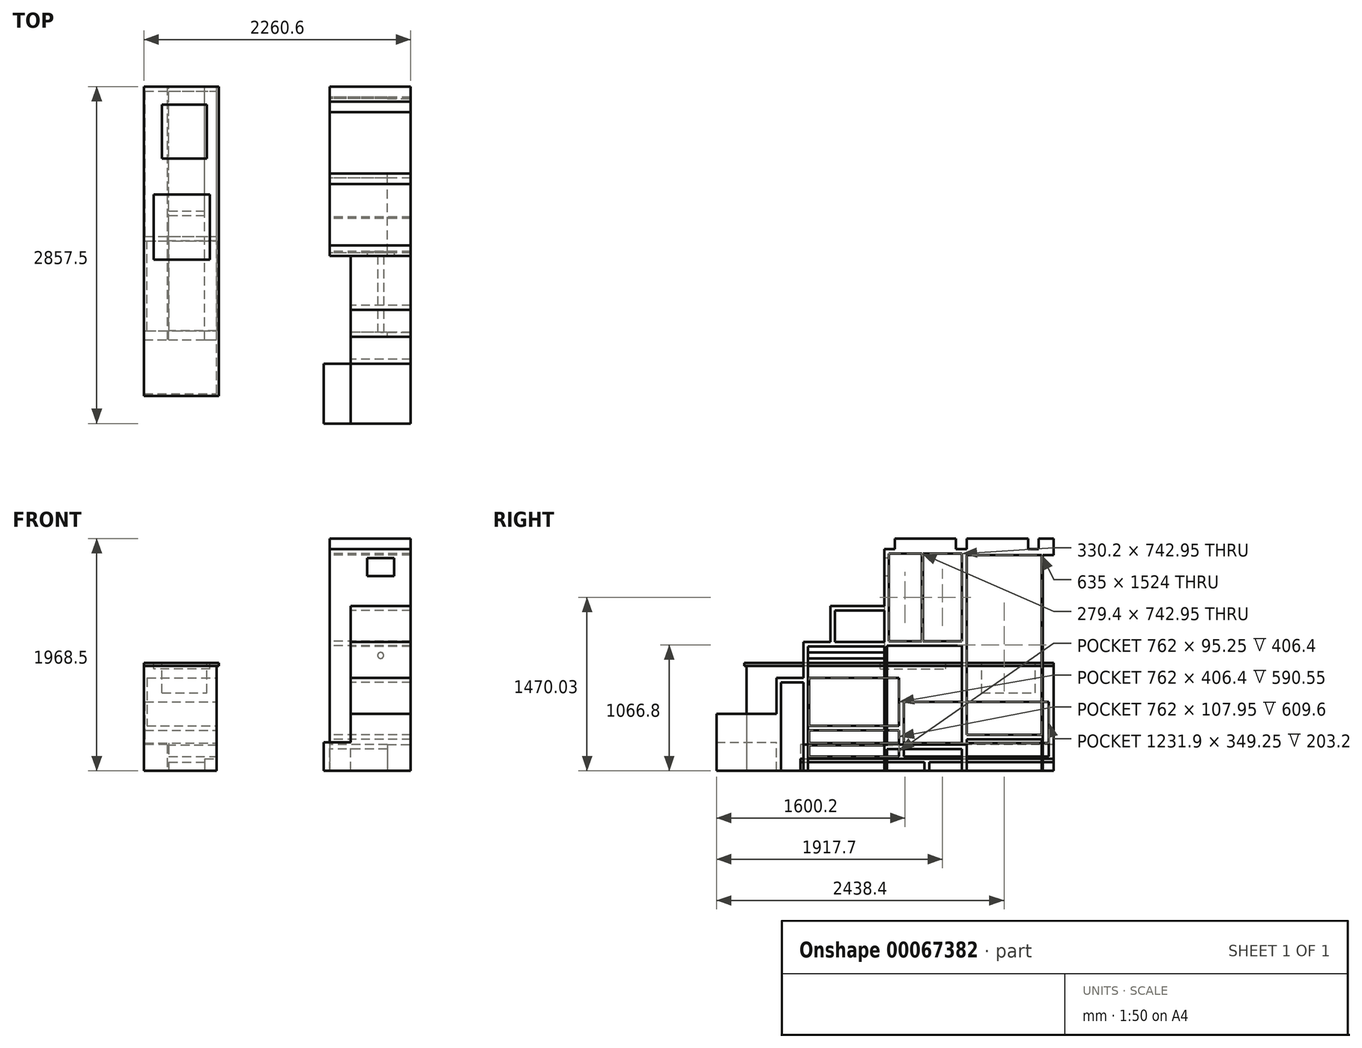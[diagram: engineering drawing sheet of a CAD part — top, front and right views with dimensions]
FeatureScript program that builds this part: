
annotation { "Feature Type Name" : "Feature", "Feature Type Description" : "" }
export const myFeature = defineFeature(function(context is Context, id is Id, definition is map)
    precondition{}
    {
        {
            var Q0;
            Q0=qCreatedBy(makeId("Top.planeOp"),FACE);
            var sketch = newSketch(context, id + "F0", { "sketchPlane" : qUnion([Q0])});
            skLineSegment(sketch, "E0", {"start": v(0, 0) * mm, "end": v(635, 0) * mm});
            skLineSegment(sketch, "E1", {"start": v(635, 0) * mm, "end": v(635, -2146.3) * mm});
            skLineSegment(sketch, "E2", {"start": v(635, -2146.3) * mm, "end": v(0, -2146.3) * mm});
            skLineSegment(sketch, "E3", {"start": v(0, -2146.3) * mm, "end": v(0, 0) * mm});
            skLineSegment(sketch, "E4", {"start": v(0, -2146.3) * mm, "end": v(0, -3213.1) * mm, "construction": true});
            skLineSegment(sketch, "E5", {"start": v(0, -3213.1) * mm, "end": v(635, -3213.1) * mm, "construction": true});
            skLineSegment(sketch, "E6", {"start": v(635, -3213.1) * mm, "end": v(635, -2146.3) * mm, "construction": true});
            skSolve(sketch);
        }
        {
            var Q0;
            Q0 = qSketchRegion(id + "F0", true);
            extrude(context, id + "F1", {"entities" : qUnion([Q0]), "depth" : 914.4 * mm});
        }
        {
            var Q0;
            Q0=makeQuery(id+"F1.opExtrude","SWEPT_FACE",FACE,{"disambiguationData":[OSD([sQuery(id+"F0.wireOp",EDGE,"E2")])]});
            var sketch = newSketch(context, id + "F2", { "sketchPlane" : qUnion([Q0])});
            skLineSegment(sketch, "E7.bottom", {"start": v(0, 0) * mm, "end": v(196.85, 0) * mm});
            skLineSegment(sketch, "E7.top", {"start": v(0, 222.25) * mm, "end": v(196.85, 222.25) * mm});
            skLineSegment(sketch, "E7.left", {"start": v(0, 0) * mm, "end": v(0, 222.25) * mm});
            skLineSegment(sketch, "E7.right", {"start": v(196.85, 0) * mm, "end": v(196.85, 222.25) * mm});
            skSolve(sketch);
        }
        {
            var Q0;
            Q0 = qSketchRegion(id + "F2", true);
            extrude(context, id + "F3", {"entities" : qUnion([Q0]), "operationType" : NewBodyOperationType.REMOVE, "oppositeDirection" : true, "depth" : 2260.6 * mm});
        }
        {
            var Q0;
            Q0=makeQuery(id+"F1.opExtrude","CAP_FACE",FACE,{"disambiguationData":[OSD([sQuery(id+"F0.wireOp",EDGE,"E0"),sQuery(id+"F0.wireOp",EDGE,"L1nPwehb-1XyT-S8cI-bZGU-SJZBOORDtoRi"),sQuery(id+"F0.wireOp",EDGE,"4dkKAuYr-NdsE-A3nL-FX6l-y6qERZtvD3tl"),sQuery(id+"F0.wireOp",EDGE,"E1"),sQuery(id+"F0.wireOp",EDGE,"E2"),sQuery(id+"F0.wireOp",EDGE,"E3")])],"isStart":true});
            var sketch = newSketch(context, id + "F4", { "sketchPlane" : qUnion([Q0])});
            skLineSegment(sketch, "E8", {"start": v(615.95, 2146.3) * mm, "end": v(615.95, 0) * mm});
            skLineSegment(sketch, "E9", {"start": v(615.95, 0) * mm, "end": v(635, 0) * mm});
            skLineSegment(sketch, "E10", {"start": v(635, 0) * mm, "end": v(635, 2146.3) * mm});
            skLineSegment(sketch, "E11", {"start": v(635, 2146.3) * mm, "end": v(615.95, 2146.3) * mm});
            skSolve(sketch);
        }
        {
            var Q0;
            Q0 = qSketchRegion(id + "F4", true);
            extrude(context, id + "F5", {"entities" : qUnion([Q0]), "operationType" : NewBodyOperationType.REMOVE, "oppositeDirection" : true, "depth" : 889 * mm});
        }
        {
            var Q0;
            Q0=makeQuery(id+"F1.opExtrude","SWEPT_FACE",FACE,{"disambiguationData":[OSD([sQuery(id+"F0.wireOp",EDGE,"E2")])]});
            var sketch = newSketch(context, id + "F6", { "sketchPlane" : qUnion([Q0])});
            skLineSegment(sketch, "E12.bottom", {"start": v(635, 889) * mm, "end": v(0, 889) * mm});
            skLineSegment(sketch, "E12.top", {"start": v(635, 914.4) * mm, "end": v(0, 914.4) * mm});
            skLineSegment(sketch, "E12.left", {"start": v(635, 889) * mm, "end": v(635, 914.4) * mm});
            skLineSegment(sketch, "E12.right", {"start": v(0, 889) * mm, "end": v(0, 914.4) * mm});
            skSolve(sketch);
        }
        {
            var Q0;
            Q0=makeQuery(id+"F1.opExtrude","CAP_FACE",FACE,{"disambiguationData":[OSD([sQuery(id+"F0.wireOp",EDGE,"E0"),sQuery(id+"F0.wireOp",EDGE,"L1nPwehb-1XyT-S8cI-bZGU-SJZBOORDtoRi"),sQuery(id+"F0.wireOp",EDGE,"4dkKAuYr-NdsE-A3nL-FX6l-y6qERZtvD3tl"),sQuery(id+"F0.wireOp",EDGE,"E1"),sQuery(id+"F0.wireOp",EDGE,"E2"),sQuery(id+"F0.wireOp",EDGE,"E3")])],"isStart":false});
            var sketch = newSketch(context, id + "F7", { "sketchPlane" : qUnion([Q0])});
            skLineSegment(sketch, "E13.bottom", {"start": v(558.8, -1466.85) * mm, "end": v(82.55, -1466.85) * mm});
            skLineSegment(sketch, "E13.top", {"start": v(558.8, -914.4) * mm, "end": v(82.55, -914.4) * mm});
            skLineSegment(sketch, "E13.left", {"start": v(558.8, -1466.85) * mm, "end": v(558.8, -914.4) * mm});
            skLineSegment(sketch, "E13.right", {"start": v(82.55, -1466.85) * mm, "end": v(82.55, -914.4) * mm});
            skSolve(sketch);
        }
        {
            var Q0;
            Q0 = qSketchRegion(id + "F7", true);
            extrude(context, id + "F8", {"entities" : qUnion([Q0]), "operationType" : NewBodyOperationType.REMOVE, "oppositeDirection" : true, "depth" : 50.8 * mm});
        }
        {
            var Q0;
            Q0=makeQuery(id+"F1.opExtrude","SWEPT_FACE",FACE,{"disambiguationData":[OSD([sQuery(id+"F0.wireOp",EDGE,"E1")])]});
            var sketch = newSketch(context, id + "F9", { "sketchPlane" : qUnion([Q0])});
            skLineSegment(sketch, "E14.bottom", {"start": v(-2070.1, 787.4) * mm, "end": v(-1308.1, 787.4) * mm});
            skLineSegment(sketch, "E14.top", {"start": v(-2070.1, 381) * mm, "end": v(-1308.1, 381) * mm});
            skLineSegment(sketch, "E14.left", {"start": v(-2070.1, 787.4) * mm, "end": v(-2070.1, 381) * mm});
            skLineSegment(sketch, "E14.right", {"start": v(-1308.1, 787.4) * mm, "end": v(-1308.1, 381) * mm});
            skLineSegment(sketch, "E15", {"start": v(-1689.1, 787.4) * mm, "end": v(-1190.62, 914.4) * mm, "construction": true});
            skSolve(sketch);
        }
        {
            var Q0;
            Q0 = qSketchRegion(id + "F9", true);
            extrude(context, id + "F10", {"entities" : qUnion([Q0]), "operationType" : NewBodyOperationType.REMOVE, "oppositeDirection" : true, "depth" : 609.6 * mm});
        }
        {
            var Q0;
            Q0=makeQuery(id+"F6nNggxzTz6gh16_2.boolean.opBoolean","MERGE",FACE,{"derivedFrom":[makeQuery(id+"F1.opExtrude","CAP_FACE",FACE,{"disambiguationData":[OSD([sQuery(id+"F0.wireOp",EDGE,"E0"),sQuery(id+"F0.wireOp",EDGE,"L1nPwehb-1XyT-S8cI-bZGU-SJZBOORDtoRi"),sQuery(id+"F0.wireOp",EDGE,"4dkKAuYr-NdsE-A3nL-FX6l-y6qERZtvD3tl"),sQuery(id+"F0.wireOp",EDGE,"E1"),sQuery(id+"F0.wireOp",EDGE,"E2"),sQuery(id+"F0.wireOp",EDGE,"E3")])],"isStart":false}),makeQuery(id+"F6nNggxzTz6gh16_2.opExtrude","SWEPT_FACE",FACE,{"disambiguationData":[OSD([sQuery(id+"F6.wireOp",EDGE,"E12.top")])]})]});
            var sketch = newSketch(context, id + "F11", { "sketchPlane" : qUnion([Q0])});
            skLineSegment(sketch, "E16.bottom", {"start": v(152.4, -609.6) * mm, "end": v(533.4, -609.6) * mm});
            skLineSegment(sketch, "E16.top", {"start": v(152.4, -152.4) * mm, "end": v(533.4, -152.4) * mm});
            skLineSegment(sketch, "E16.left", {"start": v(152.4, -609.6) * mm, "end": v(152.4, -152.4) * mm});
            skLineSegment(sketch, "E16.right", {"start": v(533.4, -609.6) * mm, "end": v(533.4, -152.4) * mm});
            skSolve(sketch);
        }
        {
            var Q0;
            Q0 = qSketchRegion(id + "F11", true);
            extrude(context, id + "F12", {"entities" : qUnion([Q0]), "operationType" : NewBodyOperationType.REMOVE, "oppositeDirection" : true, "depth" : 254 * mm});
        }
        {
            var Q0;
            Q0=makeQuery(id+"F5.boolean.opBoolean","COPY",FACE,{"derivedFrom":makeQuery(id+"F5.opExtrude","SWEPT_FACE",FACE,{"disambiguationData":[OSD([sQuery(id+"F4.wireOp",EDGE,"E8")])]})});
            var sketch = newSketch(context, id + "F13", { "sketchPlane" : qUnion([Q0])});
            skLineSegment(sketch, "E17.bottom", {"start": v(-2146.3, 0) * mm, "end": v(0, 0) * mm});
            skLineSegment(sketch, "E17.top", {"start": v(-2146.3, 101.6) * mm, "end": v(0, 101.6) * mm});
            skLineSegment(sketch, "E17.left", {"start": v(-2146.3, 0) * mm, "end": v(-2146.3, 101.6) * mm});
            skLineSegment(sketch, "E17.right", {"start": v(0, 0) * mm, "end": v(0, 101.6) * mm});
            skSolve(sketch);
        }
        {
            var Q0;
            Q0 = qSketchRegion(id + "F13", true);
            extrude(context, id + "F14", {"entities" : qUnion([Q0]), "operationType" : NewBodyOperationType.REMOVE, "oppositeDirection" : true, "depth" : 101.6 * mm});
        }
        {
            var Q0;
            Q0=makeQuery(id+"F5.boolean.opBoolean","COPY",FACE,{"derivedFrom":makeQuery(id+"F5.opExtrude","SWEPT_FACE",FACE,{"disambiguationData":[OSD([sQuery(id+"F4.wireOp",EDGE,"E8")])]})});
            var sketch = newSketch(context, id + "F15", { "sketchPlane" : qUnion([Q0])});
            skLineSegment(sketch, "E18.bottom", {"start": v(-2070.1, 342.9) * mm, "end": v(-1308.1, 342.9) * mm});
            skLineSegment(sketch, "E18.top", {"start": v(-2070.1, 120.65) * mm, "end": v(-1308.1, 120.65) * mm});
            skLineSegment(sketch, "E18.left", {"start": v(-2070.1, 342.9) * mm, "end": v(-2070.1, 120.65) * mm});
            skLineSegment(sketch, "E18.right", {"start": v(-1308.1, 342.9) * mm, "end": v(-1308.1, 120.65) * mm});
            skLineSegment(sketch, "E19.bottom", {"start": v(-1270, 584.2) * mm, "end": v(-38.1, 584.2) * mm});
            skLineSegment(sketch, "E19.top", {"start": v(-1270, 120.65) * mm, "end": v(-38.1, 120.65) * mm});
            skLineSegment(sketch, "E19.left", {"start": v(-1270, 584.2) * mm, "end": v(-1270, 120.65) * mm});
            skLineSegment(sketch, "E19.right", {"start": v(-38.1, 584.2) * mm, "end": v(-38.1, 120.65) * mm});
            skSolve(sketch);
        }
        {
            var Q0;
            Q0 = qSketchRegion(id + "F15", true);
            extrude(context, id + "F16", {"entities" : qUnion([Q0]), "operationType" : NewBodyOperationType.REMOVE, "oppositeDirection" : true, "depth" : 406.4 * mm});
        }
        {
            var Q0;
            Q0=makeQuery(id+"F16.boolean.opBoolean","COPY",FACE,{"derivedFrom":makeQuery(id+"F16.opExtrude","CAP_FACE",FACE,{"disambiguationData":[OSD([sQuery(id+"F15.wireOp",EDGE,"E18.bottom"),sQuery(id+"F15.wireOp",EDGE,"E18.top"),sQuery(id+"F15.wireOp",EDGE,"E18.left"),sQuery(id+"F15.wireOp",EDGE,"E18.right")])],"isStart":false})});
            var sketch = newSketch(context, id + "F17", { "sketchPlane" : qUnion([Q0])});
            skLineSegment(sketch, "E20.bottom", {"start": v(-2070.1, 342.9) * mm, "end": v(-1308.1, 342.9) * mm});
            skLineSegment(sketch, "E20.top", {"start": v(-2070.1, 234.95) * mm, "end": v(-1308.1, 234.95) * mm});
            skLineSegment(sketch, "E20.left", {"start": v(-2070.1, 342.9) * mm, "end": v(-2070.1, 234.95) * mm});
            skLineSegment(sketch, "E20.right", {"start": v(-1308.1, 342.9) * mm, "end": v(-1308.1, 234.95) * mm});
            skLineSegment(sketch, "E21", {"start": v(-1270, 584.2) * mm, "end": v(-1270, 234.95) * mm});
            skLineSegment(sketch, "E22", {"start": v(-1270, 234.95) * mm, "end": v(-38.1, 234.95) * mm});
            skLineSegment(sketch, "E23", {"start": v(-38.1, 234.95) * mm, "end": v(-38.1, 584.2) * mm});
            skLineSegment(sketch, "E24", {"start": v(-38.1, 584.2) * mm, "end": v(-1270, 584.2) * mm});
            skSolve(sketch);
        }
        {
            var Q0;
            Q0 = qSketchRegion(id + "F17", true);
            extrude(context, id + "F18", {"entities" : qUnion([Q0]), "operationType" : NewBodyOperationType.REMOVE, "oppositeDirection" : true, "depth" : 203.2 * mm});
        }
        {
            var Q0;
            Q0=makeQuery(id+"F16.boolean.opBoolean","COPY",FACE,{"derivedFrom":makeQuery(id+"F16.opExtrude","CAP_FACE",FACE,{"disambiguationData":[OSD([sQuery(id+"F15.wireOp",EDGE,"E18.bottom"),sQuery(id+"F15.wireOp",EDGE,"E18.top"),sQuery(id+"F15.wireOp",EDGE,"E18.left"),sQuery(id+"F15.wireOp",EDGE,"E18.right")])],"isStart":false})});
            var sketch = newSketch(context, id + "F19", { "sketchPlane" : qUnion([Q0])});
            skLineSegment(sketch, "E25.bottom", {"start": v(-1308.1, 234.95) * mm, "end": v(-2070.1, 234.95) * mm});
            skLineSegment(sketch, "E25.top", {"start": v(-1308.1, 215.9) * mm, "end": v(-2070.1, 215.9) * mm});
            skLineSegment(sketch, "E25.left", {"start": v(-1308.1, 234.95) * mm, "end": v(-1308.1, 215.9) * mm});
            skLineSegment(sketch, "E25.right", {"start": v(-2070.1, 234.95) * mm, "end": v(-2070.1, 215.9) * mm});
            skSolve(sketch);
        }
        {
            var Q0;
            Q0 = qSketchRegion(id + "F19", true);
            var Q1;
            Q1=makeQuery(id+"F5.boolean.opBoolean","COPY",FACE,{"derivedFrom":makeQuery(id+"F5.opExtrude","SWEPT_FACE",FACE,{"disambiguationData":[OSD([sQuery(id+"F4.wireOp",EDGE,"E8")])]})});
            extrude(context, id + "F20", {"entities" : qUnion([Q0]), "operationType" : NewBodyOperationType.ADD, "endBound" : BoundingType.UP_TO_SURFACE, "endBoundEntityFace" : qUnion([Q1]), "depth" : 25.4 * mm});
        }
        {
            var Q0;
            Q0=makeQuery(id+"F14.boolean.opBoolean","COPY",FACE,{"derivedFrom":makeQuery(id+"F14.opExtrude","CAP_FACE",FACE,{"disambiguationData":[OSD([sQuery(id+"F13.wireOp",EDGE,"E17.bottom"),sQuery(id+"F13.wireOp",EDGE,"E17.top"),sQuery(id+"F13.wireOp",EDGE,"E17.left"),sQuery(id+"F13.wireOp",EDGE,"E17.right")])],"isStart":false})});
            var sketch = newSketch(context, id + "F21", { "sketchPlane" : qUnion([Q0])});
            skLineSegment(sketch, "E26.bottom", {"start": v(-2146.3, 73.19) * mm, "end": v(-1092.2, 73.19) * mm});
            skLineSegment(sketch, "E26.top", {"start": v(-2146.3, 0) * mm, "end": v(-1092.2, 0) * mm});
            skLineSegment(sketch, "E26.left", {"start": v(-2146.3, 73.19) * mm, "end": v(-2146.3, 0) * mm});
            skLineSegment(sketch, "E26.right", {"start": v(-1092.2, 73.19) * mm, "end": v(-1092.2, 0) * mm});
            skLineSegment(sketch, "E27.bottom", {"start": v(-1054.1, 73.19) * mm, "end": v(0, 73.19) * mm});
            skLineSegment(sketch, "E27.top", {"start": v(-1054.1, 0) * mm, "end": v(0, 0) * mm});
            skLineSegment(sketch, "E27.left", {"start": v(0, 73.19) * mm, "end": v(0, 0) * mm});
            skLineSegment(sketch, "E27.right", {"start": v(-1054.1, 73.19) * mm, "end": v(-1054.1, 0) * mm});
            skSolve(sketch);
        }
        {
            var Q0;
            Q0 = qSketchRegion(id + "F21", true);
            extrude(context, id + "F22", {"entities" : qUnion([Q0]), "operationType" : NewBodyOperationType.REMOVE, "oppositeDirection" : true, "depth" : 304.8 * mm});
        }
        {
            var Q0;
            Q0=qCreatedBy(makeId("Top.planeOp"),FACE);
            var sketch = newSketch(context, id + "F23", { "sketchPlane" : qUnion([Q0])});
            skLineSegment(sketch, "E28.bottom", {"start": v(2260.6, 0) * mm, "end": v(1574.8, 0) * mm});
            skLineSegment(sketch, "E28.top", {"start": v(2260.6, -2146.3) * mm, "end": v(1574.8, -2146.3) * mm});
            skLineSegment(sketch, "E28.left", {"start": v(2260.6, 0) * mm, "end": v(2260.6, -2146.3) * mm});
            skLineSegment(sketch, "E28.right", {"start": v(1574.8, 0) * mm, "end": v(1574.8, -2146.3) * mm});
            skSolve(sketch);
        }
        {
            var Q0;
            Q0 = qSketchRegion(id + "F23", true);
            extrude(context, id + "F24", {"entities" : qUnion([Q0]), "depth" : 1879.6 * mm});
        }
        {
            var Q0;
            Q0=makeQuery(id+"F1.opExtrude","SWEPT_FACE",FACE,{"disambiguationData":[OSD([sQuery(id+"F0.wireOp",EDGE,"E2")])]});
            var sketch = newSketch(context, id + "F25", { "sketchPlane" : qUnion([Q0])});
            skLineSegment(sketch, "E29.bottom", {"start": v(0, 914.4) * mm, "end": v(635, 914.4) * mm});
            skLineSegment(sketch, "E29.top", {"start": v(0, 0) * mm, "end": v(615.95, 0) * mm});
            skLineSegment(sketch, "E29.left", {"start": v(0, 914.4) * mm, "end": v(0, 0) * mm});
            skLineSegment(sketch, "E29.right", {"start": v(615.95, 889) * mm, "end": v(615.95, 0) * mm});
            skLineSegment(sketch, "E30.top", {"start": v(615.95, 889) * mm, "end": v(635, 889) * mm});
            skLineSegment(sketch, "E30.right", {"start": v(635, 914.4) * mm, "end": v(635, 889) * mm});
            skSolve(sketch);
        }
        {
            var Q0;
            Q0 = qSketchRegion(id + "F25", true);
            var Q1;
            Q1=makeQuery(id+"FPw9wNljHIeiaqn_1.opExtrude","SWEPT_FACE",FACE,{"disambiguationData":[OSD([sQuery(id+"F2S1z9t6CFDuZh9_1.wireOp",EDGE,"fWxXcAP5-6dmd-jM5E-bbKU-4OgyUSsTFvBE")])]});
            extrude(context, id + "F26", {"entities" : qUnion([Q0]), "operationType" : NewBodyOperationType.ADD, "endBoundEntityFace" : qUnion([Q1]), "depth" : 457.2 * mm});
        }
        {
            var Q0;
            Q0=makeQuery(id+"F26.opExtrude","CAP_FACE",FACE,{"disambiguationData":[OSD([sQuery(id+"F25.wireOp",EDGE,"E29.bottom"),sQuery(id+"F25.wireOp",EDGE,"E29.top"),sQuery(id+"F25.wireOp",EDGE,"E29.left"),sQuery(id+"F25.wireOp",EDGE,"E29.right"),sQuery(id+"F25.wireOp",EDGE,"E30.top"),sQuery(id+"F25.wireOp",EDGE,"E30.right")])],"isStart":false});
            var sketch = newSketch(context, id + "F27", { "sketchPlane" : qUnion([Q0])});
            skLineSegment(sketch, "E31.bottom", {"start": v(0, 914.4) * mm, "end": v(635, 914.4) * mm});
            skLineSegment(sketch, "E31.top", {"start": v(0, 889) * mm, "end": v(635, 889) * mm});
            skLineSegment(sketch, "E31.left", {"start": v(0, 914.4) * mm, "end": v(0, 889) * mm});
            skLineSegment(sketch, "E31.right", {"start": v(635, 914.4) * mm, "end": v(635, 889) * mm});
            skSolve(sketch);
        }
        {
            var Q0;
            Q0 = qSketchRegion(id + "F27", true);
            extrude(context, id + "F28", {"entities" : qUnion([Q0]), "operationType" : NewBodyOperationType.ADD, "depth" : 19.05 * mm});
        }
        {
            var Q0;
            Q0=makeQuery(id+"F24.opExtrude","SWEPT_FACE",FACE,{"disambiguationData":[OSD([sQuery(id+"F23.wireOp",EDGE,"E28.right")])]});
            var sketch = newSketch(context, id + "F29", { "sketchPlane" : qUnion([Q0])});
            skLineSegment(sketch, "E32.bottom", {"start": v(101.6, 1828.8) * mm, "end": v(736.6, 1828.8) * mm});
            skLineSegment(sketch, "E32.top", {"start": v(101.6, 304.8) * mm, "end": v(736.6, 304.8) * mm});
            skLineSegment(sketch, "E32.left", {"start": v(101.6, 1828.8) * mm, "end": v(101.6, 304.8) * mm});
            skLineSegment(sketch, "E32.right", {"start": v(736.6, 1828.8) * mm, "end": v(736.6, 304.8) * mm});
            skSolve(sketch);
        }
        {
            var Q0;
            Q0 = qSketchRegion(id + "F29", true);
            extrude(context, id + "F30", {"entities" : qUnion([Q0]), "operationType" : NewBodyOperationType.REMOVE, "endBound" : BoundingType.THROUGH_ALL, "oppositeDirection" : true, "depth" : 25.4 * mm});
        }
        {
            var Q0;
            {var subQ2=sQuery(id+"F23.wireOp",EDGE,"E28.bottom");Q0=makeQuery(id+"F30.boolean.opBoolean","SPLIT",FACE,{"disambiguationData":[TD([makeQuery(id+"F30.opExtrude","SWEPT_FACE",FACE,{"disambiguationData":[OSD([sQuery(id+"F29.wireOp",EDGE,"E32.top")])]})])],"derivedFrom":makeQuery(id+"F24.opExtrude","SWEPT_FACE",FACE,{"disambiguationData":[OSD([subQ2])]})});}
            var sketch = newSketch(context, id + "F31", { "sketchPlane" : qUnion([Q0])});
            skLineSegment(sketch, "E33.bottom", {"start": v(-2260.6, 0) * mm, "end": v(-2063.75, 0) * mm});
            skLineSegment(sketch, "E33.top", {"start": v(-2260.6, 222.25) * mm, "end": v(-2063.75, 222.25) * mm});
            skLineSegment(sketch, "E33.left", {"start": v(-2260.6, 0) * mm, "end": v(-2260.6, 222.25) * mm});
            skLineSegment(sketch, "E33.right", {"start": v(-2063.75, 0) * mm, "end": v(-2063.75, 222.25) * mm});
            skSolve(sketch);
        }
        {
            var Q0;
            Q0 = qSketchRegion(id + "F31", true);
            extrude(context, id + "F32", {"entities" : qUnion([Q0]), "operationType" : NewBodyOperationType.REMOVE, "endBound" : BoundingType.THROUGH_ALL, "oppositeDirection" : true, "depth" : 25.4 * mm});
        }
        {
            var Q0;
            Q0=makeQuery(id+"F24.opExtrude","SWEPT_FACE",FACE,{"disambiguationData":[OSD([sQuery(id+"F23.wireOp",EDGE,"E28.right")])]});
            var sketch = newSketch(context, id + "F33", { "sketchPlane" : qUnion([Q0])});
            skLineSegment(sketch, "E34.bottom", {"start": v(88.9, 0) * mm, "end": v(0, 0) * mm});
            skLineSegment(sketch, "E34.top", {"start": v(88.9, 1828.8) * mm, "end": v(0, 1828.8) * mm});
            skLineSegment(sketch, "E34.left", {"start": v(88.9, 0) * mm, "end": v(88.9, 1828.8) * mm});
            skLineSegment(sketch, "E34.right", {"start": v(0, 0) * mm, "end": v(0, 1828.8) * mm});
            skSolve(sketch);
        }
        {
            var Q0;
            Q0 = qSketchRegion(id + "F33", true);
            extrude(context, id + "F34", {"entities" : qUnion([Q0]), "operationType" : NewBodyOperationType.REMOVE, "endBound" : BoundingType.THROUGH_ALL, "oppositeDirection" : true, "depth" : 25.4 * mm});
        }
        {
            var Q0;
            Q0=makeQuery(id+"F24.opExtrude","SWEPT_FACE",FACE,{"disambiguationData":[OSD([sQuery(id+"F23.wireOp",EDGE,"E28.right")])]});
            var sketch = newSketch(context, id + "F35", { "sketchPlane" : qUnion([Q0])});
            skLineSegment(sketch, "E35.bottom", {"start": v(1892.3, 1397) * mm, "end": v(1435.1, 1397) * mm});
            skLineSegment(sketch, "E35.top", {"start": v(2146.3, 2006.6) * mm, "end": v(1435.1, 2006.6) * mm});
            skLineSegment(sketch, "E35.left", {"start": v(2146.3, 1092.2) * mm, "end": v(2146.3, 2006.6) * mm});
            skLineSegment(sketch, "E35.right", {"start": v(1435.1, 1397) * mm, "end": v(1435.1, 2006.6) * mm});
            skLineSegment(sketch, "E36.top", {"start": v(2146.3, 1092.2) * mm, "end": v(1892.3, 1092.2) * mm});
            skLineSegment(sketch, "E36.right", {"start": v(1892.3, 1397) * mm, "end": v(1892.3, 1092.2) * mm});
            skSolve(sketch);
        }
        {
            var Q0;
            Q0 = qSketchRegion(id + "F35", true);
            extrude(context, id + "F36", {"entities" : qUnion([Q0]), "operationType" : NewBodyOperationType.REMOVE, "endBound" : BoundingType.THROUGH_ALL, "oppositeDirection" : true, "depth" : 25.4 * mm});
        }
        {
            var Q0;
            Q0=makeQuery(id+"F24.opExtrude","SWEPT_FACE",FACE,{"disambiguationData":[OSD([sQuery(id+"F23.wireOp",EDGE,"E28.top")])]});
            var sketch = newSketch(context, id + "F37", { "sketchPlane" : qUnion([Q0])});
            skLineSegment(sketch, "E37.bottom", {"start": v(2260.6, 1092.2) * mm, "end": v(1574.8, 1092.2) * mm});
            skLineSegment(sketch, "E37.top", {"start": v(2260.6, 0) * mm, "end": v(1574.8, 0) * mm});
            skLineSegment(sketch, "E37.left", {"start": v(2260.6, 1092.2) * mm, "end": v(2260.6, 0) * mm});
            skLineSegment(sketch, "E37.right", {"start": v(1574.8, 1092.2) * mm, "end": v(1574.8, 0) * mm});
            skSolve(sketch);
        }
        {
            var Q0;
            Q0 = qSketchRegion(id + "F37", true);
            extrude(context, id + "F38", {"entities" : qUnion([Q0]), "operationType" : NewBodyOperationType.ADD, "depth" : 711.2 * mm});
        }
        {
            var Q0;
            Q0=makeQuery(id+"F38.boolean.opBoolean","MERGE",FACE,{"derivedFrom":[makeQuery(id+"F24.opExtrude","SWEPT_FACE",FACE,{"disambiguationData":[OSD([sQuery(id+"F23.wireOp",EDGE,"E28.right")])]}),makeQuery(id+"F38.opExtrude","SWEPT_FACE",FACE,{"disambiguationData":[OSD([sQuery(id+"F37.wireOp",EDGE,"E37.right")])]})]});
            var sketch = newSketch(context, id + "F39", { "sketchPlane" : qUnion([Q0])});
            skLineSegment(sketch, "E38.bottom", {"start": v(2857.5, 1092.2) * mm, "end": v(2120.9, 1092.2) * mm});
            skLineSegment(sketch, "E38.top", {"start": v(2857.5, 787.4) * mm, "end": v(2120.9, 787.4) * mm});
            skLineSegment(sketch, "E38.left", {"start": v(2857.5, 1092.2) * mm, "end": v(2857.5, 787.4) * mm});
            skLineSegment(sketch, "E38.right", {"start": v(2120.9, 1092.2) * mm, "end": v(2120.9, 787.4) * mm});
            skLineSegment(sketch, "E39.bottom", {"start": v(2857.5, 787.4) * mm, "end": v(2349.5, 787.4) * mm});
            skLineSegment(sketch, "E39.top", {"start": v(2857.5, 482.6) * mm, "end": v(2349.5, 482.6) * mm});
            skLineSegment(sketch, "E39.left", {"start": v(2857.5, 787.4) * mm, "end": v(2857.5, 482.6) * mm});
            skLineSegment(sketch, "E39.right", {"start": v(2349.5, 787.4) * mm, "end": v(2349.5, 482.6) * mm});
            skSolve(sketch);
        }
        {
            var Q0;
            Q0 = qSketchRegion(id + "F39", true);
            extrude(context, id + "F40", {"entities" : qUnion([Q0]), "operationType" : NewBodyOperationType.REMOVE, "endBound" : BoundingType.THROUGH_ALL, "oppositeDirection" : true, "depth" : 25.4 * mm});
        }
        {
            var Q0;
            Q0=makeQuery(id+"F38.boolean.opBoolean","MERGE",FACE,{"derivedFrom":[makeQuery(id+"F24.opExtrude","SWEPT_FACE",FACE,{"disambiguationData":[OSD([sQuery(id+"F23.wireOp",EDGE,"E28.right")])]}),makeQuery(id+"F38.opExtrude","SWEPT_FACE",FACE,{"disambiguationData":[OSD([sQuery(id+"F37.wireOp",EDGE,"E37.right")])]})]});
            var sketch = newSketch(context, id + "F41", { "sketchPlane" : qUnion([Q0])});
            skLineSegment(sketch, "E40.bottom", {"start": v(774.7, 222.25) * mm, "end": v(1409.7, 222.25) * mm});
            skLineSegment(sketch, "E40.top", {"start": v(774.7, 1060.45) * mm, "end": v(1409.7, 1060.45) * mm});
            skLineSegment(sketch, "E40.left", {"start": v(774.7, 222.25) * mm, "end": v(774.7, 1060.45) * mm});
            skLineSegment(sketch, "E40.right", {"start": v(1409.7, 222.25) * mm, "end": v(1409.7, 1060.45) * mm});
            skSolve(sketch);
        }
        {
            var Q0;
            Q0 = qSketchRegion(id + "F41", true);
            extrude(context, id + "F42", {"entities" : qUnion([Q0]), "operationType" : NewBodyOperationType.REMOVE, "endBound" : BoundingType.THROUGH_ALL, "oppositeDirection" : true, "depth" : 25.4 * mm});
        }
        {
            var Q0;
            Q0=makeQuery(id+"F38.boolean.opBoolean","MERGE",FACE,{"derivedFrom":[makeQuery(id+"F24.opExtrude","SWEPT_FACE",FACE,{"disambiguationData":[OSD([sQuery(id+"F23.wireOp",EDGE,"E28.right")])]}),makeQuery(id+"F38.opExtrude","SWEPT_FACE",FACE,{"disambiguationData":[OSD([sQuery(id+"F37.wireOp",EDGE,"E37.right")])]})]});
            var sketch = newSketch(context, id + "F43", { "sketchPlane" : qUnion([Q0])});
            skLineSegment(sketch, "E41", {"start": v(1892.3, 1092.2) * mm, "end": v(2120.9, 1092.2) * mm});
            skLineSegment(sketch, "E42", {"start": v(2120.9, 1092.2) * mm, "end": v(2120.9, 787.4) * mm});
            skLineSegment(sketch, "E43", {"start": v(2120.9, 787.4) * mm, "end": v(2349.5, 787.4) * mm});
            skLineSegment(sketch, "E44", {"start": v(2349.5, 787.4) * mm, "end": v(2349.5, 482.6) * mm});
            skLineSegment(sketch, "E45", {"start": v(2349.5, 482.6) * mm, "end": v(2857.5, 482.6) * mm});
            skLineSegment(sketch, "E46", {"start": v(2857.5, 482.6) * mm, "end": v(2857.5, 0) * mm});
            skLineSegment(sketch, "E47", {"start": v(2857.5, 0) * mm, "end": v(1435.1, 0) * mm});
            skLineSegment(sketch, "E48", {"start": v(1892.3, 1092.2) * mm, "end": v(1892.3, 1397) * mm});
            skLineSegment(sketch, "E49", {"start": v(1892.3, 1397) * mm, "end": v(1435.1, 1397) * mm});
            skLineSegment(sketch, "E50", {"start": v(1435.1, 1397) * mm, "end": v(1435.1, 0) * mm});
            skSolve(sketch);
        }
        {
            var Q0;
            Q0 = qSketchRegion(id + "F43", true);
            extrude(context, id + "F44", {"entities" : qUnion([Q0]), "operationType" : NewBodyOperationType.REMOVE, "oppositeDirection" : true, "depth" : 177.8 * mm});
        }
        {
            var Q0;
            Q0=makeQuery(id+"F44.boolean.opBoolean","COPY",FACE,{"derivedFrom":makeQuery(id+"F44.opExtrude","CAP_FACE",FACE,{"disambiguationData":[OSD([sQuery(id+"F43.wireOp",EDGE,"E41"),sQuery(id+"F43.wireOp",EDGE,"E42"),sQuery(id+"F43.wireOp",EDGE,"E43"),sQuery(id+"F43.wireOp",EDGE,"E44"),sQuery(id+"F43.wireOp",EDGE,"E45"),sQuery(id+"F43.wireOp",EDGE,"E46"),sQuery(id+"F43.wireOp",EDGE,"E47"),sQuery(id+"F43.wireOp",EDGE,"YasEaaFj-X7v1-acRF-2n8C-2obE4N0J3St1")])],"isStart":false})});
            var sketch = newSketch(context, id + "F45", { "sketchPlane" : qUnion([Q0])});
            skLineSegment(sketch, "E51.bottom", {"start": v(2857.5, 0) * mm, "end": v(2349.5, 0) * mm});
            skLineSegment(sketch, "E51.top", {"start": v(2857.5, 241.3) * mm, "end": v(2349.5, 241.3) * mm});
            skLineSegment(sketch, "E51.left", {"start": v(2857.5, 0) * mm, "end": v(2857.5, 241.3) * mm});
            skLineSegment(sketch, "E51.right", {"start": v(2349.5, 0) * mm, "end": v(2349.5, 241.3) * mm});
            skLineSegment(sketch, "E52", {"start": v(2857.5, 241.3) * mm, "end": v(2857.5, 482.6) * mm, "construction": true});
            skSolve(sketch);
        }
        {
            var Q0;
            Q0 = qSketchRegion(id + "F45", true);
            extrude(context, id + "F46", {"entities" : qUnion([Q0]), "operationType" : NewBodyOperationType.ADD, "depth" : 228.6 * mm});
        }
        {
            var Q0;
            Q0=makeQuery(id+"F38.boolean.opBoolean","MERGE",FACE,{"derivedFrom":[makeQuery(id+"F24.opExtrude","SWEPT_FACE",FACE,{"disambiguationData":[OSD([sQuery(id+"F23.wireOp",EDGE,"E28.right")])]}),makeQuery(id+"F38.opExtrude","SWEPT_FACE",FACE,{"disambiguationData":[OSD([sQuery(id+"F37.wireOp",EDGE,"E37.right")])]})]});
            var sketch = newSketch(context, id + "F47", { "sketchPlane" : qUnion([Q0])});
            skLineSegment(sketch, "E53.bottom", {"start": v(1397, 1098.55) * mm, "end": v(1117.6, 1098.55) * mm});
            skLineSegment(sketch, "E53.top", {"start": v(1397, 1841.5) * mm, "end": v(1117.6, 1841.5) * mm});
            skLineSegment(sketch, "E53.left", {"start": v(1397, 1098.55) * mm, "end": v(1397, 1841.5) * mm});
            skLineSegment(sketch, "E53.right", {"start": v(1117.6, 1098.55) * mm, "end": v(1117.6, 1841.5) * mm});
            skLineSegment(sketch, "E54.bottom", {"start": v(774.7, 1841.5) * mm, "end": v(1104.9, 1841.5) * mm});
            skLineSegment(sketch, "E54.top", {"start": v(774.7, 1098.55) * mm, "end": v(1104.9, 1098.55) * mm});
            skLineSegment(sketch, "E54.left", {"start": v(774.7, 1841.5) * mm, "end": v(774.7, 1098.55) * mm});
            skLineSegment(sketch, "E54.right", {"start": v(1104.9, 1841.5) * mm, "end": v(1104.9, 1098.55) * mm});
            skSolve(sketch);
        }
        {
            var Q0;
            Q0 = qSketchRegion(id + "F47", true);
            extrude(context, id + "F48", {"entities" : qUnion([Q0]), "operationType" : NewBodyOperationType.REMOVE, "endBound" : BoundingType.THROUGH_ALL, "oppositeDirection" : true, "depth" : 25.4 * mm});
        }
        {
            var Q0;
            Q0=makeQuery(id+"F44.boolean.opBoolean","MERGE",FACE,{"derivedFrom":[makeQuery(id+"F36.boolean.opBoolean","COPY",FACE,{"derivedFrom":makeQuery(id+"F36.opExtrude","SWEPT_FACE",FACE,{"disambiguationData":[OSD([sQuery(id+"F35.wireOp",EDGE,"E35.right")])]})}),makeQuery(id+"F44.opExtrude","SWEPT_FACE",FACE,{"disambiguationData":[OSD([sQuery(id+"F43.wireOp",EDGE,"E50")])]})]});
            var sketch = newSketch(context, id + "F49", { "sketchPlane" : qUnion([Q0])});
            skLineSegment(sketch, "E55.bottom", {"start": v(2120.9, 1803.4) * mm, "end": v(1892.3, 1803.4) * mm});
            skLineSegment(sketch, "E55.top", {"start": v(2120.9, 1651) * mm, "end": v(1892.3, 1651) * mm});
            skLineSegment(sketch, "E55.left", {"start": v(2120.9, 1803.4) * mm, "end": v(2120.9, 1651) * mm});
            skLineSegment(sketch, "E55.right", {"start": v(1892.3, 1803.4) * mm, "end": v(1892.3, 1651) * mm});
            skLineSegment(sketch, "E56", {"start": v(2006.6, 1397) * mm, "end": v(2006.6, 1651) * mm, "construction": true});
            skSolve(sketch);
        }
        {
            var Q0;
            Q0 = qSketchRegion(id + "F49", true);
            extrude(context, id + "F50", {"entities" : qUnion([Q0]), "operationType" : NewBodyOperationType.REMOVE, "endBound" : BoundingType.UP_TO_NEXT, "oppositeDirection" : true, "depth" : 25.4 * mm});
        }
        {
            var Q0;
            Q0=makeQuery(id+"F44.boolean.opBoolean","COPY",FACE,{"derivedFrom":makeQuery(id+"F44.opExtrude","CAP_FACE",FACE,{"disambiguationData":[OSD([sQuery(id+"F43.wireOp",EDGE,"E41"),sQuery(id+"F43.wireOp",EDGE,"E42"),sQuery(id+"F43.wireOp",EDGE,"E43"),sQuery(id+"F43.wireOp",EDGE,"E44"),sQuery(id+"F43.wireOp",EDGE,"E45"),sQuery(id+"F43.wireOp",EDGE,"E46"),sQuery(id+"F43.wireOp",EDGE,"E47"),sQuery(id+"F43.wireOp",EDGE,"E48"),sQuery(id+"F43.wireOp",EDGE,"E49"),sQuery(id+"F43.wireOp",EDGE,"E50")])],"isStart":false})});
            var sketch = newSketch(context, id + "F51", { "sketchPlane" : qUnion([Q0])});
            skLineSegment(sketch, "E57.bottom", {"start": v(2311.4, 749.3) * mm, "end": v(2120.9, 749.3) * mm});
            skLineSegment(sketch, "E57.top", {"start": v(2311.4, 0) * mm, "end": v(2120.9, 0) * mm});
            skLineSegment(sketch, "E57.left", {"start": v(2311.4, 749.3) * mm, "end": v(2311.4, 0) * mm});
            skLineSegment(sketch, "E57.right", {"start": v(2120.9, 749.3) * mm, "end": v(2120.9, 0) * mm});
            skLineSegment(sketch, "E58.bottom", {"start": v(1435.1, 1054.1) * mm, "end": v(2082.8, 1054.1) * mm});
            skLineSegment(sketch, "E58.top", {"start": v(1435.1, 0) * mm, "end": v(2082.8, 0) * mm});
            skLineSegment(sketch, "E58.left", {"start": v(1435.1, 1054.1) * mm, "end": v(1435.1, 0) * mm});
            skLineSegment(sketch, "E58.right", {"start": v(2082.8, 1054.1) * mm, "end": v(2082.8, 0) * mm});
            skLineSegment(sketch, "E59.bottom", {"start": v(1435.1, 1358.9) * mm, "end": v(1854.2, 1358.9) * mm});
            skLineSegment(sketch, "E59.top", {"start": v(1435.1, 1092.2) * mm, "end": v(1854.2, 1092.2) * mm});
            skLineSegment(sketch, "E59.left", {"start": v(1435.1, 1358.9) * mm, "end": v(1435.1, 1092.2) * mm});
            skLineSegment(sketch, "E59.right", {"start": v(1854.2, 1358.9) * mm, "end": v(1854.2, 1092.2) * mm});
            skSolve(sketch);
        }
        {
            var Q0;
            Q0 = qSketchRegion(id + "F51", true);
            extrude(context, id + "F52", {"entities" : qUnion([Q0]), "operationType" : NewBodyOperationType.REMOVE, "endBound" : BoundingType.THROUGH_ALL, "oppositeDirection" : true, "depth" : 25.4 * mm});
        }
        {
            var Q0;
            Q0=makeQuery(id+"F52.boolean.opBoolean","COPY",FACE,{"derivedFrom":makeQuery(id+"F52.opExtrude","SWEPT_FACE",FACE,{"disambiguationData":[OSD([sQuery(id+"F51.wireOp",EDGE,"E58.right")])]})});
            var sketch = newSketch(context, id + "F53", { "sketchPlane" : qUnion([Q0])});
            skCircle(sketch, "E60", {"center": v(-2006.6, 977.9) * mm, "radius": 25.4 * mm});
            skLineSegment(sketch, "E61", {"start": v(-2006.6, 1054.1) * mm, "end": v(-2006.6, 977.9) * mm, "construction": true});
            skSolve(sketch);
        }
        {
            var Q0;
            Q0 = qSketchRegion(id + "F53", true);
            extrude(context, id + "F54", {"entities" : qUnion([Q0]), "operationType" : NewBodyOperationType.ADD, "endBound" : BoundingType.UP_TO_NEXT, "depth" : 25.4 * mm});
        }
        {
            var Q0;
            Q0=makeQuery(id+"F38.boolean.opBoolean","MERGE",FACE,{"derivedFrom":[makeQuery(id+"F24.opExtrude","SWEPT_FACE",FACE,{"disambiguationData":[OSD([sQuery(id+"F23.wireOp",EDGE,"E28.right")])]}),makeQuery(id+"F38.opExtrude","SWEPT_FACE",FACE,{"disambiguationData":[OSD([sQuery(id+"F37.wireOp",EDGE,"E37.right")])]})]});
            var sketch = newSketch(context, id + "F55", { "sketchPlane" : qUnion([Q0])});
            skLineSegment(sketch, "E62.bottom", {"start": v(101.6, 266.7) * mm, "end": v(736.6, 266.7) * mm});
            skLineSegment(sketch, "E62.top", {"start": v(101.6, 0) * mm, "end": v(736.6, 0) * mm});
            skLineSegment(sketch, "E62.left", {"start": v(101.6, 266.7) * mm, "end": v(101.6, 0) * mm});
            skLineSegment(sketch, "E62.right", {"start": v(736.6, 266.7) * mm, "end": v(736.6, 0) * mm});
            skLineSegment(sketch, "E63.bottom", {"start": v(774.7, 184.15) * mm, "end": v(1409.7, 184.15) * mm});
            skLineSegment(sketch, "E63.top", {"start": v(774.7, 0) * mm, "end": v(1409.7, 0) * mm});
            skLineSegment(sketch, "E63.left", {"start": v(774.7, 184.15) * mm, "end": v(774.7, 0) * mm});
            skLineSegment(sketch, "E63.right", {"start": v(1409.7, 184.15) * mm, "end": v(1409.7, 0) * mm});
            skSolve(sketch);
        }
        {
            var Q0;
            Q0 = qSketchRegion(id + "F55", true);
            extrude(context, id + "F56", {"entities" : qUnion([Q0]), "operationType" : NewBodyOperationType.REMOVE, "endBound" : BoundingType.THROUGH_ALL, "oppositeDirection" : true, "depth" : 25.4 * mm});
        }
        {
            var Q0;
            Q0=makeQuery(id+"F38.boolean.opBoolean","MERGE",FACE,{"derivedFrom":[makeQuery(id+"F24.opExtrude","SWEPT_FACE",FACE,{"disambiguationData":[OSD([sQuery(id+"F23.wireOp",EDGE,"E28.right")])]}),makeQuery(id+"F38.opExtrude","SWEPT_FACE",FACE,{"disambiguationData":[OSD([sQuery(id+"F37.wireOp",EDGE,"E37.right")])]})]});
            var sketch = newSketch(context, id + "F57", { "sketchPlane" : qUnion([Q0])});
            skLineSegment(sketch, "E64", {"start": v(1346.2, 1879.6) * mm, "end": v(1346.2, 1968.5) * mm});
            skLineSegment(sketch, "E65", {"start": v(1346.2, 1968.5) * mm, "end": v(825.5, 1968.5) * mm});
            skLineSegment(sketch, "E66", {"start": v(825.5, 1968.5) * mm, "end": v(825.5, 1879.6) * mm});
            skLineSegment(sketch, "E67", {"start": v(825.5, 1879.6) * mm, "end": v(1346.2, 1879.6) * mm});
            skLineSegment(sketch, "E68", {"start": v(736.6, 1879.6) * mm, "end": v(736.6, 1968.5) * mm});
            skLineSegment(sketch, "E69", {"start": v(736.6, 1968.5) * mm, "end": v(215.9, 1968.5) * mm});
            skLineSegment(sketch, "E70", {"start": v(215.9, 1968.5) * mm, "end": v(215.9, 1879.6) * mm});
            skLineSegment(sketch, "E71", {"start": v(215.9, 1879.6) * mm, "end": v(736.6, 1879.6) * mm});
            skLineSegment(sketch, "E72.bottom", {"start": v(0, 1879.6) * mm, "end": v(127, 1879.6) * mm});
            skLineSegment(sketch, "E72.top", {"start": v(0, 1968.5) * mm, "end": v(127, 1968.5) * mm});
            skLineSegment(sketch, "E72.left", {"start": v(0, 1879.6) * mm, "end": v(0, 1968.5) * mm});
            skLineSegment(sketch, "E72.right", {"start": v(127, 1879.6) * mm, "end": v(127, 1968.5) * mm});
            skLineSegment(sketch, "E73", {"start": v(127, 1879.6) * mm, "end": v(215.9, 1879.6) * mm, "construction": true});
            skLineSegment(sketch, "E74", {"start": v(736.6, 1879.6) * mm, "end": v(825.5, 1879.6) * mm, "construction": true});
            skLineSegment(sketch, "E75", {"start": v(1346.2, 1879.6) * mm, "end": v(1435.1, 1879.6) * mm, "construction": true});
            skSolve(sketch);
        }
        {
            var Q0;
            Q0 = qSketchRegion(id + "F57", true);
            var Q1;
            Q1=makeQuery(id+"F38.boolean.opBoolean","MERGE",FACE,{"derivedFrom":[makeQuery(id+"F24.opExtrude","SWEPT_FACE",FACE,{"disambiguationData":[OSD([sQuery(id+"F23.wireOp",EDGE,"E28.left")])]}),makeQuery(id+"F38.opExtrude","SWEPT_FACE",FACE,{"disambiguationData":[OSD([sQuery(id+"F37.wireOp",EDGE,"E37.left")])]})]});
            extrude(context, id + "F58", {"entities" : qUnion([Q0]), "operationType" : NewBodyOperationType.ADD, "endBound" : BoundingType.UP_TO_SURFACE, "oppositeDirection" : true, "endBoundEntityFace" : qUnion([Q1]), "depth" : 25.4 * mm});
        }
    });
